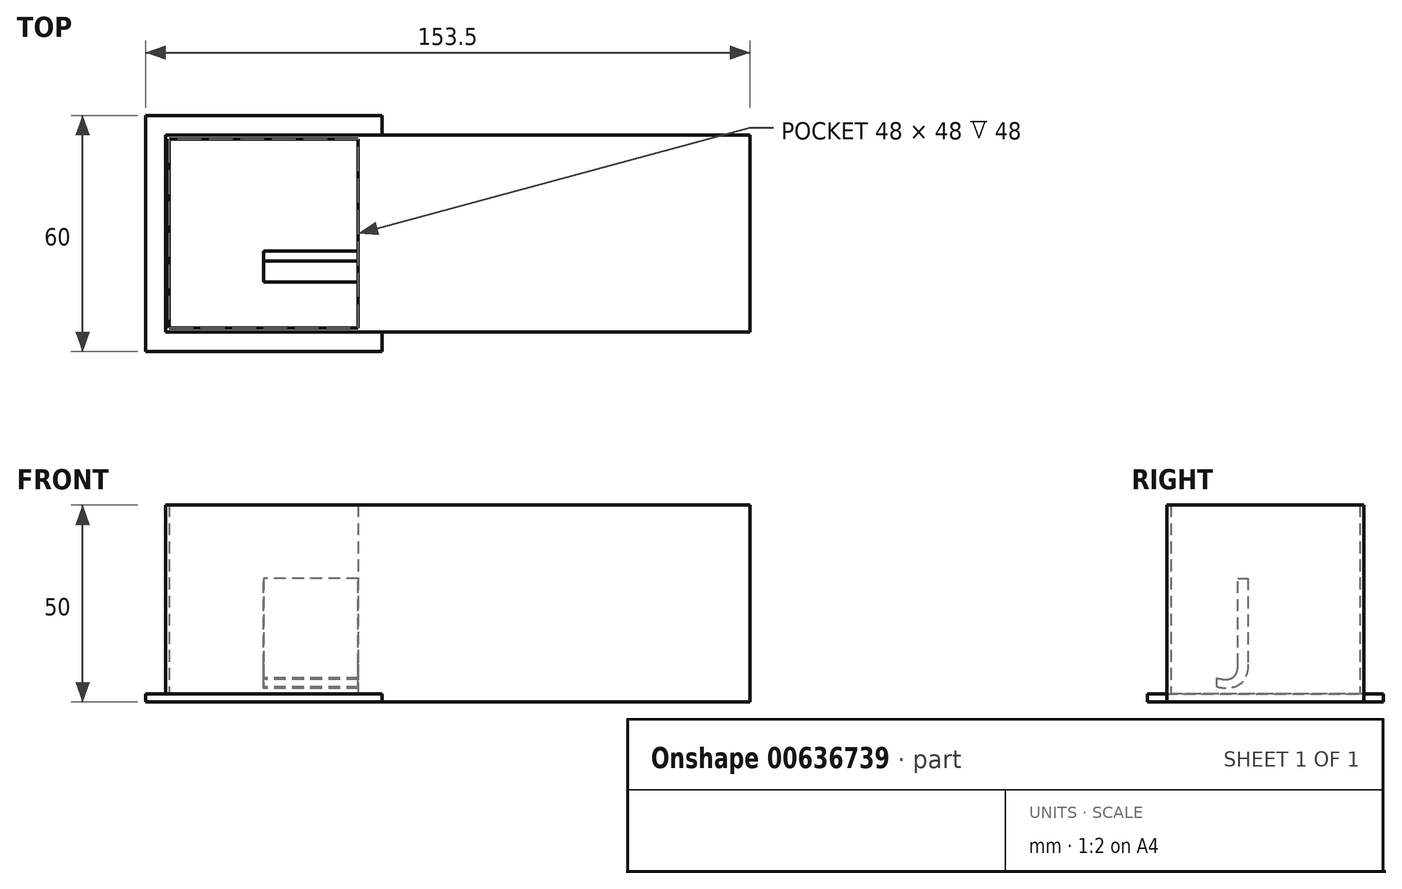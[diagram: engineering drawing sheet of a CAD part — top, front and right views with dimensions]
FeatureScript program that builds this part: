
annotation { "Feature Type Name" : "Feature", "Feature Type Description" : "" }
export const myFeature = defineFeature(function(context is Context, id is Id, definition is map)
    precondition{}
    {
        {
            var Q0;
            Q0=qCreatedBy(makeId("Top.planeOp"),FACE);
            var sketch = newSketch(context, id + "F0", { "sketchPlane" : qUnion([Q0])});
            skLineSegment(sketch, "E0.bottom", {"start": v(-30, -30) * mm, "end": v(30, -30) * mm});
            skLineSegment(sketch, "E0.top", {"start": v(-30, 30) * mm, "end": v(30, 30) * mm});
            skLineSegment(sketch, "E0.left", {"start": v(-30, -30) * mm, "end": v(-30, 30) * mm});
            skLineSegment(sketch, "E0.right", {"start": v(30, -30) * mm, "end": v(30, 30) * mm});
            skPoint(sketch, "E0.middle", {"position": v(0, 0) * mm});
            skSolve(sketch);
        }
        {
            var Q0;
            Q0 = qSketchRegion(id + "F0", true);
            extrude(context, id + "F1", {"entities" : qUnion([Q0]), "depth" : 2 * mm, "offsetDistance" : 25 * mm});
        }
        {
            var Q0;
            Q0=qCreatedBy(makeId("Top.planeOp"),FACE);
            var sketch = newSketch(context, id + "F2", { "sketchPlane" : qUnion([Q0])});
            skLineSegment(sketch, "E1.bottom", {"start": v(-25, -25) * mm, "end": v(25, -25) * mm});
            skLineSegment(sketch, "E1.top", {"start": v(-25, 25) * mm, "end": v(25, 25) * mm});
            skLineSegment(sketch, "E1.left", {"start": v(-25, -25) * mm, "end": v(-25, 25) * mm});
            skLineSegment(sketch, "E1.right", {"start": v(25, -25) * mm, "end": v(25, 25) * mm});
            skPoint(sketch, "E1.middle", {"position": v(0, 0) * mm});
            skLineSegment(sketch, "E2.bottom", {"start": v(-24, -24) * mm, "end": v(24, -24) * mm});
            skLineSegment(sketch, "E2.top", {"start": v(-24, 24) * mm, "end": v(24, 24) * mm});
            skLineSegment(sketch, "E2.left", {"start": v(-24, -24) * mm, "end": v(-24, 24) * mm});
            skLineSegment(sketch, "E2.right", {"start": v(24, -24) * mm, "end": v(24, 24) * mm});
            skSolve(sketch);
        }
        {
            var Q0;
            Q0=makeQuery(id+"F2.imprint","IMPRINT",FACE,{"disambiguationData":[TD([[makeQuery(id+"F2.imprint","IMPRINT",EDGE,{"derivedFrom":sQuery(id+"F2.wireOp",EDGE,"E1.bottom")}),1.0]])]});
            extrude(context, id + "F3", {"entities" : qUnion([Q0]), "depth" : 50 * mm, "offsetDistance" : 25 * mm});
        }
        {
            var Q0;
            Q0=qCreatedBy(makeId("Right.planeOp"),FACE);
            var sketch = newSketch(context, id + "F4", { "sketchPlane" : qUnion([Q0])});
            skText(sketch, "E3", { "text": "J", "fontName": "OpenSans-Regular.ttf"});
            const initialGuessF4  = {"E3": [-0.00988, 0.00928, 1, 0, 0.02233]};
            skSetInitialGuess(sketch, initialGuessF4);
            skSolve(sketch);
        }
        {
            var Q0;
            Q0 = qSketchRegion(id + "F4", true);
            var Q1;
            Q1=makeQuery(id+"F3.opExtrude","SWEPT_FACE",FACE,{"disambiguationData":[OSD([sQuery(id+"F2.wireOp",EDGE,"E1.right")])]});
            extrude(context, id + "F5", {"entities" : qUnion([Q0, Q1]), "operationType" : NewBodyOperationType.ADD, "endBound" : BoundingType.THROUGH_ALL, "depth" : 25 * mm, "offsetDistance" : 25 * mm});
        }
    });
